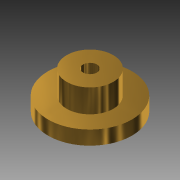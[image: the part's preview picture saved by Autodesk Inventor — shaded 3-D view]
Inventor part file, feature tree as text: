
AUTODESK INVENTOR PART (.ipt)
format: ipt  version: 2015 (Build 190159000, 159)  size: 109,056 bytes
history: native  units: mm
features: extrude x3, sketch x3, other x1
ambient origin geometry x8: Origin, YZ Plane, XZ Plane, XY Plane, X Axis, Y Axis, Z Axis, Center Point
bodies: Body1 (feature_tree)
feature tree (7):
  other  "ソリッド1"
  extrude  "押し出し1"  Depth=18.0mm
  extrude  "押し出し2"  Depth=3.0mm TaperAngle=0.0deg
  extrude  "押し出し3"  Depth=10.0mm
  sketch  "スケッチ1"
  sketch  "スケッチ2"
  sketch  "スケッチ3"
